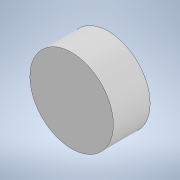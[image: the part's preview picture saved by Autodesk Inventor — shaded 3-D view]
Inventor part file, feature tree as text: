
AUTODESK INVENTOR PART (.ipt)
format: ipt  version: 2021 (Build 250183000, 183)  size: 89,600 bytes
history: native  units: mm
features: extrude x1, sketch x1
ambient origin geometry x8: Origin, YZ Plane, XZ Plane, XY Plane, X Axis, Y Axis, Z Axis, Center Point
bodies: Solid1 (feature_tree)
feature tree (2):
  extrude  "Extrusion1"  Depth=33.0mm TaperAngle=0.0deg
  sketch  "Sketch1"  dims[d0=75.0mm d1=33.0mm d2=0.0mm]
